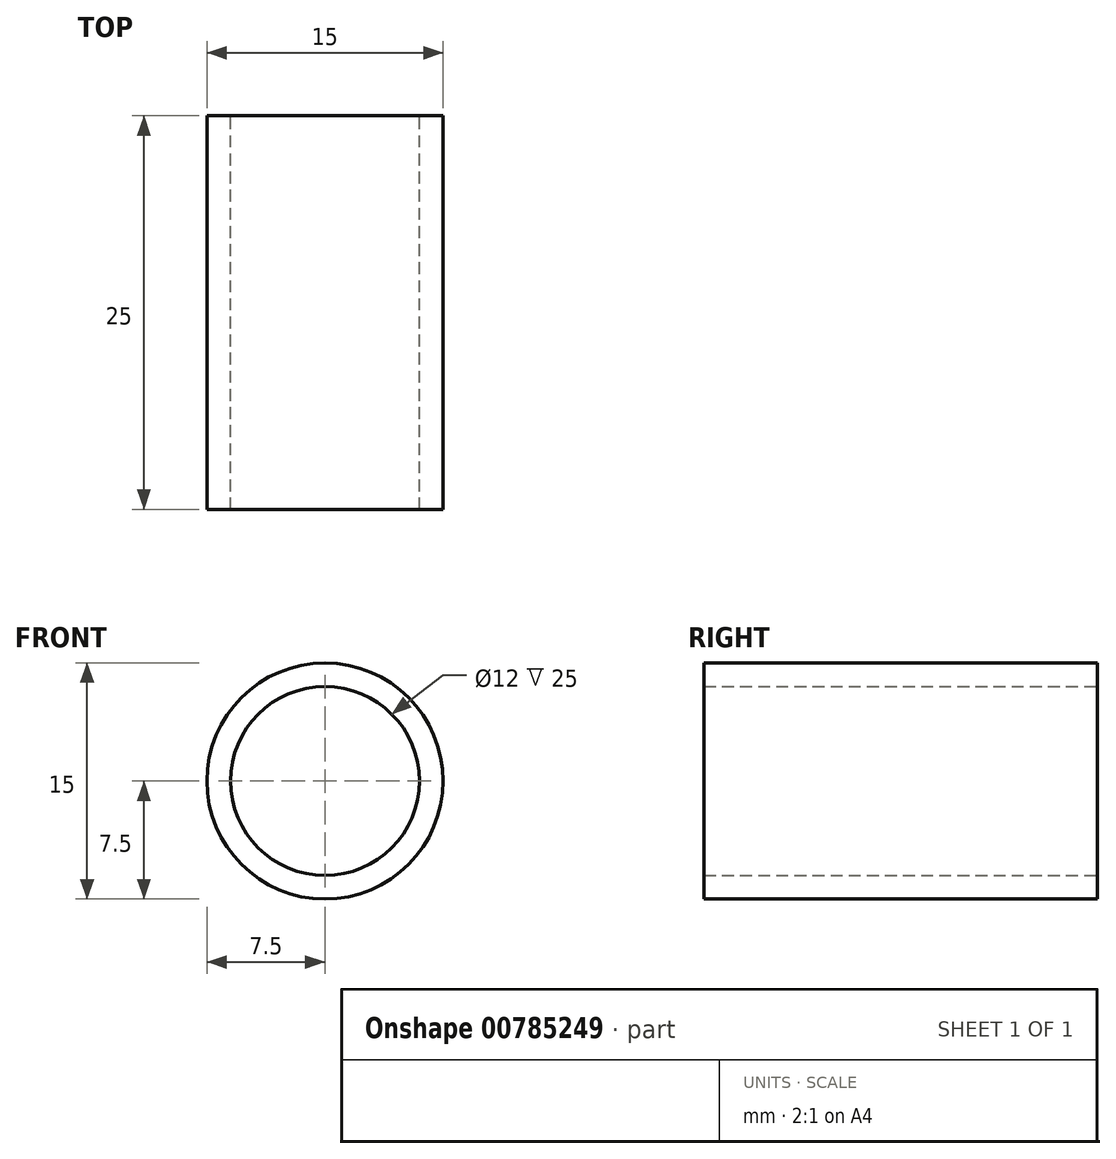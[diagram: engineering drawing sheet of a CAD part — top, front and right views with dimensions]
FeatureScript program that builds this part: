
annotation { "Feature Type Name" : "Feature", "Feature Type Description" : "" }
export const myFeature = defineFeature(function(context is Context, id is Id, definition is map)
    precondition{}
    {
        {
            var Q0;
            Q0=qCreatedBy(makeId("Front.planeOp"),FACE);
            var sketch = newSketch(context, id + "F0", { "sketchPlane" : qUnion([Q0])});
            skCircle(sketch, "E0", {"center": v(0, 0) * mm, "radius": 6 * mm});
            skCircle(sketch, "E1", {"center": v(0, 0) * mm, "radius": 7.5 * mm});
            skSolve(sketch);
        }
        {
            var Q0;
            Q0=makeQuery(id+"F0.imprint","IMPRINT",FACE,{"disambiguationData":[TD([[makeQuery(id+"F0.imprint","IMPRINT",EDGE,{"derivedFrom":sQuery(id+"F0.wireOp",EDGE,"E0")}),-1.0]])]});
            extrude(context, id + "F1", {"entities" : qUnion([Q0]), "depth" : 25 * mm, "offsetDistance" : 25 * mm});
        }
    });
